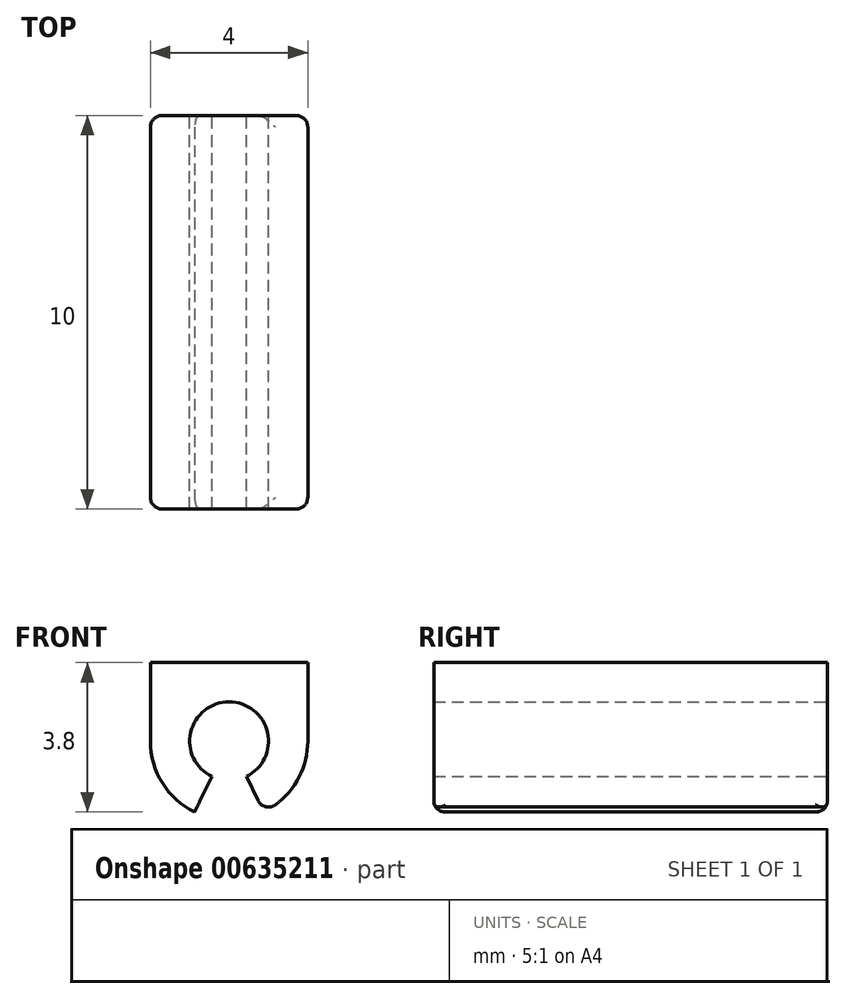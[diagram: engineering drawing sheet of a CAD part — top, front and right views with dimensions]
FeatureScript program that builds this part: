
annotation { "Feature Type Name" : "Feature", "Feature Type Description" : "" }
export const myFeature = defineFeature(function(context is Context, id is Id, definition is map)
    precondition{}
    {
        {
            var Q0;
            Q0=qCreatedBy(makeId("Front.planeOp"),FACE);
            var sketch = newSketch(context, id + "F0", { "sketchPlane" : qUnion([Q0])});
            skCircle(sketch, "E0", {"center": v(0, 0) * mm, "radius": 1 * mm});
            skArc(sketch, "E1", {"start": v(-2, 0) * mm, "mid": v(0, -2) * mm, "end": v(2, 0) * mm});
            skLineSegment(sketch, "E2", {"start": v(-2, 0) * mm, "end": v(-2, 2) * mm});
            skLineSegment(sketch, "E3", {"start": v(-2, 2) * mm, "end": v(0, 2) * mm});
            skLineSegment(sketch, "E4.MirrorCS", {"start": v(2, 2) * mm, "end": v(0, 2) * mm});
            skLineSegment(sketch, "E5.MirrorCS", {"start": v(2, 0) * mm, "end": v(2, 2) * mm});
            skSolve(sketch);
        }
        {
            var Q0;
            Q0=makeQuery(id+"F0.imprint","IMPRINT",FACE,{"disambiguationData":[TD([[makeQuery(id+"F0.imprint","IMPRINT",EDGE,{"derivedFrom":sQuery(id+"F0.wireOp",EDGE,"E0")}),-1.0]])]});
            extrude(context, id + "F1", {"entities" : qUnion([Q0]), "endBound" : BoundingType.SYMMETRIC, "depth" : 10 * mm, "offsetDistance" : 25.4 * mm});
        }
        {
            var Q0;
            Q0=makeQuery(id+"F1.opExtrude","CAP_FACE",FACE,{"disambiguationData":[OSD([sQuery(id+"F0.wireOp",EDGE,"E0"),sQuery(id+"F0.wireOp",EDGE,"E1")])],"isStart":false});
            var sketch = newSketch(context, id + "F2", { "sketchPlane" : qUnion([Q0])});
            skLineSegment(sketch, "E6", {"start": v(0, 0) * mm, "end": v(-0.87, -1.8) * mm});
            skLineSegment(sketch, "E7.MirrorCS", {"start": v(0, 0) * mm, "end": v(0.87, -1.8) * mm});
            skArc(sketch, "E8", {"start": v(-0.87, -1.8) * mm, "mid": v(0, -2) * mm, "end": v(0.87, -1.8) * mm});
            skSolve(sketch);
        }
        {
            var Q0;
            Q0=qSketchRegion(id+"F2",true);
            extrude(context, id + "F3", {"entities" : qUnion([Q0]), "operationType" : NewBodyOperationType.REMOVE, "endBound" : BoundingType.THROUGH_ALL, "oppositeDirection" : true, "depth" : 25 * mm, "offsetDistance" : 25 * mm});
        }
        {
            var Q0;
            Q0=makeQuery(id+"F3.boolean.opBoolean","COPY",EDGE,{"derivedFrom":makeQuery(id+"F3.opExtrude","SWEPT_EDGE",EDGE,{"disambiguationData":[OSD([sQuery(id+"F0.wireOp",EDGE,"E1"),sQuery(id+"F2.wireOp",EDGE,"E6"),sQuery(id+"F2.wireOp",EDGE,"E8")])]})});
            var Q1;
            Q1=makeQuery(id+"F3.boolean.opBoolean","COPY",EDGE,{"derivedFrom":makeQuery(id+"F3.opExtrude","SWEPT_EDGE",EDGE,{"disambiguationData":[OSD([sQuery(id+"F0.wireOp",EDGE,"E1"),sQuery(id+"F2.wireOp",EDGE,"E7.MirrorCS"),sQuery(id+"F2.wireOp",EDGE,"E8")])]})});
            var Q2;
            {var subQ0=sQuery(id+"F0.wireOp",EDGE,"E2");var subQ1=sQuery(id+"F0.wireOp",EDGE,"E1");Q2=makeQuery(id+"F3.boolean.opBoolean","SPLIT",EDGE,{"disambiguationData":[TD([makeQuery(id+"F1.opExtrude","SWEPT_FACE",FACE,{"disambiguationData":[OSD([subQ0])]})])],"derivedFrom":makeQuery(id+"F1.opExtrude","CAP_EDGE",EDGE,{"disambiguationData":[OSD([subQ1])],"isStart":false})});}
            var Q3;
            Q3=makeQuery(id+"F1.opExtrude","CAP_EDGE",EDGE,{"disambiguationData":[OSD([sQuery(id+"F0.wireOp",EDGE,"E2")])],"isStart":false});
            var Q4;
            {var subQ0=sQuery(id+"F0.wireOp",EDGE,"E5.MirrorCS");var subQ1=sQuery(id+"F0.wireOp",EDGE,"E1");Q4=makeQuery(id+"F3.boolean.opBoolean","SPLIT",EDGE,{"disambiguationData":[TD([makeQuery(id+"F1.opExtrude","SWEPT_FACE",FACE,{"disambiguationData":[OSD([subQ0])]})])],"derivedFrom":makeQuery(id+"F1.opExtrude","CAP_EDGE",EDGE,{"disambiguationData":[OSD([subQ1])],"isStart":false})});}
            var Q5;
            {var subQ0=sQuery(id+"F0.wireOp",EDGE,"E5.MirrorCS");var subQ1=sQuery(id+"F0.wireOp",EDGE,"E1");Q5=makeQuery(id+"F3.boolean.opBoolean","SPLIT",EDGE,{"disambiguationData":[TD([makeQuery(id+"F1.opExtrude","SWEPT_FACE",FACE,{"disambiguationData":[OSD([subQ0])]})])],"derivedFrom":makeQuery(id+"F1.opExtrude","CAP_EDGE",EDGE,{"disambiguationData":[OSD([subQ1])],"isStart":true})});}
            var Q6;
            Q6=makeQuery(id+"F1.opExtrude","CAP_EDGE",EDGE,{"disambiguationData":[OSD([sQuery(id+"F0.wireOp",EDGE,"E5.MirrorCS")])],"isStart":true});
            var Q7;
            {var subQ0=sQuery(id+"F0.wireOp",EDGE,"E2");var subQ1=sQuery(id+"F0.wireOp",EDGE,"E1");Q7=makeQuery(id+"F3.boolean.opBoolean","SPLIT",EDGE,{"disambiguationData":[TD([makeQuery(id+"F1.opExtrude","SWEPT_FACE",FACE,{"disambiguationData":[OSD([subQ0])]})])],"derivedFrom":makeQuery(id+"F1.opExtrude","CAP_EDGE",EDGE,{"disambiguationData":[OSD([subQ1])],"isStart":true})});}
            var Q8;
            Q8=makeQuery(id+"F1.opExtrude","CAP_EDGE",EDGE,{"disambiguationData":[OSD([sQuery(id+"F0.wireOp",EDGE,"E2")])],"isStart":true});
            fillet(context, id + "F4", {"entities" : qUnion([Q0, Q1, Q2, Q3, Q4, Q5, Q6, Q7, Q8]), "radius" : .3 * mm, "tangentPropagation" : true, "allowEdgeOverflow" : false});
        }
    });
